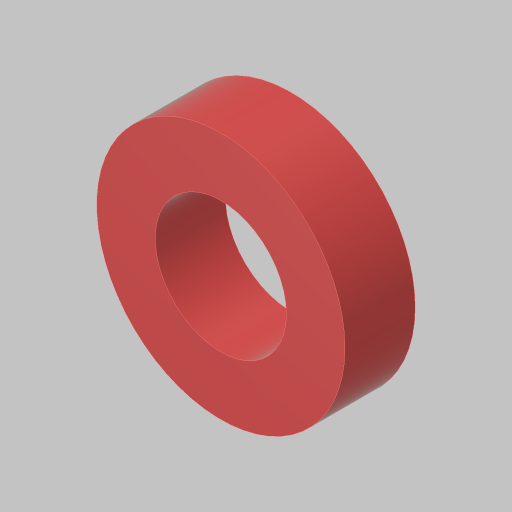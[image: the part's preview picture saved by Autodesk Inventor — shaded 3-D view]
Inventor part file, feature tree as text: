
AUTODESK INVENTOR PART (.ipt)
format: ipt  version: 2023.5 (Build 275446000, 446)  size: 111,616 bytes
history: native  units: in
note: dims shown in document units (in); Inventor stores cm internally (conversion verified against a paired STEP export)
features: extrude x1, sketch x1
ambient origin geometry x8: Origin, YZ Plane, XZ Plane, XY Plane, X Axis, Y Axis, Z Axis, Center Point
bodies: Solid1 (feature_tree)
feature tree (2):
  extrude  "Extrusion1"  Depth=0.3in
  sketch  "Sketch1"  dims[d0=0.56in d1=0.25in d2=0.3in d3=0.0in]
